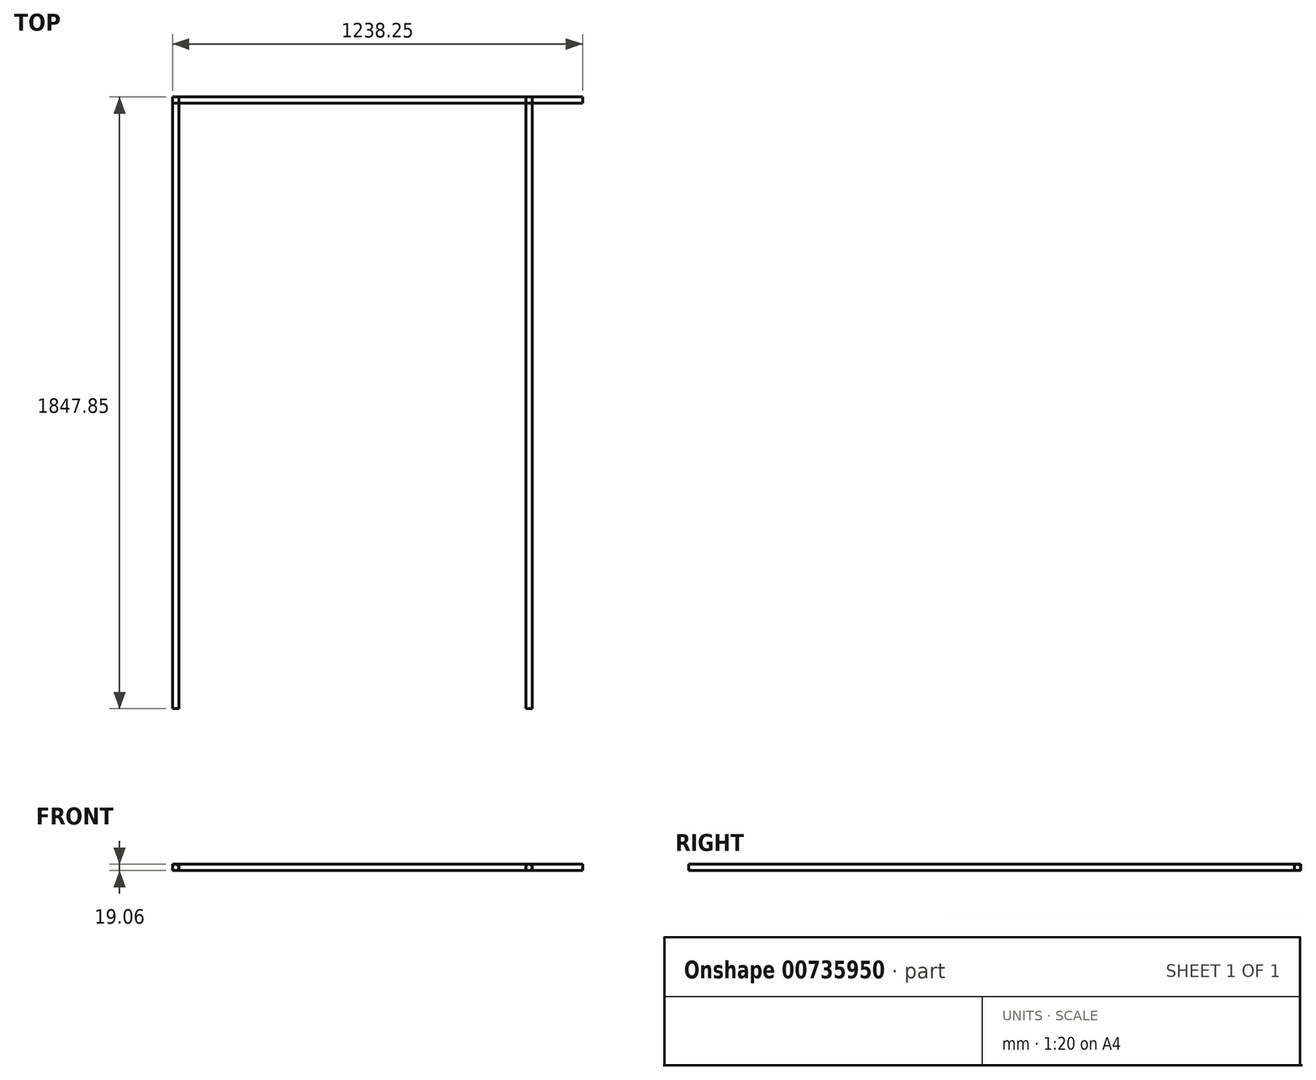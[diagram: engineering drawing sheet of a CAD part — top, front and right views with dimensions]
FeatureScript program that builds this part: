
annotation { "Feature Type Name" : "Feature", "Feature Type Description" : "" }
export const myFeature = defineFeature(function(context is Context, id is Id, definition is map)
    precondition{}
    {
        {
            var Q0;
            Q0=qCreatedBy(makeId("Front.planeOp"),FACE);
            var sketch = newSketch(context, id + "F0", { "sketchPlane" : qUnion([Q0])});
            skLineSegment(sketch, "E0", {"start": v(-36.92, 0) * mm, "end": v(1029.88, 0) * mm});
            skCircle(sketch, "E1", {"center": v(-36.92, 0) * mm, "radius": 9.53 * mm});
            skCircle(sketch, "E2", {"center": v(1029.88, 0) * mm, "radius": 9.52 * mm});
            skSolve(sketch);
        }
        {
            var Q0;
            Q0=makeQuery(id+"F0.imprint","IMPRINT",FACE,{"disambiguationData":[TD([[makeQuery(id+"F0.imprint","IMPRINT",EDGE,{"derivedFrom":sQuery(id+"F0.wireOp",EDGE,"E1")}),1.0]])]});
            var Q1;
            Q1=makeQuery(id+"F0.imprint","IMPRINT",FACE,{"disambiguationData":[TD([[makeQuery(id+"F0.imprint","IMPRINT",EDGE,{"derivedFrom":sQuery(id+"F0.wireOp",EDGE,"E2")}),1.0]])]});
            extrude(context, id + "F1", {"entities" : qUnion([Q0, Q1]), "depth" : 1828.8 * mm, "offsetDistance" : 25.4 * mm});
        }
        {
            var Q0;
            Q0=makeQuery(id+"F1.opExtrude","CAP_FACE",FACE,{"disambiguationData":[OSD([sQuery(id+"F0.wireOp",EDGE,"E2")])],"isStart":true});
            var sketch = newSketch(context, id + "F2", { "sketchPlane" : qUnion([Q0])});
            skLineSegment(sketch, "E3.bottom", {"start": v(-1020.36, -9.53) * mm, "end": v(-1039.4, -9.53) * mm});
            skLineSegment(sketch, "E3.top", {"start": v(-1020.36, 9.52) * mm, "end": v(-1039.4, 9.52) * mm});
            skLineSegment(sketch, "E3.left", {"start": v(-1020.36, -9.53) * mm, "end": v(-1020.36, 9.52) * mm});
            skLineSegment(sketch, "E3.right", {"start": v(-1039.4, -9.53) * mm, "end": v(-1039.4, 9.52) * mm});
            skPoint(sketch, "E3.middle", {"position": v(-1029.88, 0) * mm});
            skLineSegment(sketch, "E4.bottom", {"start": v(46.5, -9.53) * mm, "end": v(27.45, -9.53) * mm});
            skLineSegment(sketch, "E4.top", {"start": v(46.5, 9.53) * mm, "end": v(27.45, 9.53) * mm});
            skLineSegment(sketch, "E4.left", {"start": v(46.5, -9.52) * mm, "end": v(46.5, 9.53) * mm});
            skLineSegment(sketch, "E4.right", {"start": v(27.45, -9.53) * mm, "end": v(27.45, 9.53) * mm});
            skPoint(sketch, "E4.middle", {"position": v(36.98, 0) * mm});
            skSolve(sketch);
        }
        {
            var Q0;
            Q0 = qSketchRegion(id + "F2", true);
            extrude(context, id + "F3", {"entities" : qUnion([Q0]), "depth" : 19.05 * mm, "offsetDistance" : 25.4 * mm});
        }
        {
            var Q0;
            Q0=makeQuery(id+"F3.opExtrude","SWEPT_FACE",FACE,{"disambiguationData":[OSD([sQuery(id+"F2.wireOp",EDGE,"E4.right")])]});
            var sketch = newSketch(context, id + "F4", { "sketchPlane" : qUnion([Q0])});
            skCircle(sketch, "E5", {"center": v(9.53, 0) * mm, "radius": 9.53 * mm});
            skSolve(sketch);
        }
        {
            var Q0;
            {var subQ0=sQuery(id+"F4.wireOp",EDGE,"E5");var subQ1=sQuery(id+"F2.wireOp",EDGE,"E4.right");var subQ3=makeQuery(id+"F4.imprint","INTERSECT",VERTEX,{"derivedFrom":[makeQuery(id+"F3.opExtrude","CAP_EDGE",EDGE,{"disambiguationData":[OSD([subQ1])],"isStart":false}),subQ0]});Q0=makeQuery(id+"F4.imprint","IMPRINT",FACE,{"disambiguationData":[TD([[makeQuery(id+"F4.imprint","IMPRINT",EDGE,{"disambiguationData":[TD([[subQ3,-1.0]])],"derivedFrom":subQ0}),1.0]])]});}
            extrude(context, id + "F5", {"entities" : qUnion([Q0]), "depth" : 1219.2 * mm, "offsetDistance" : 25.4 * mm});
        }
    });
